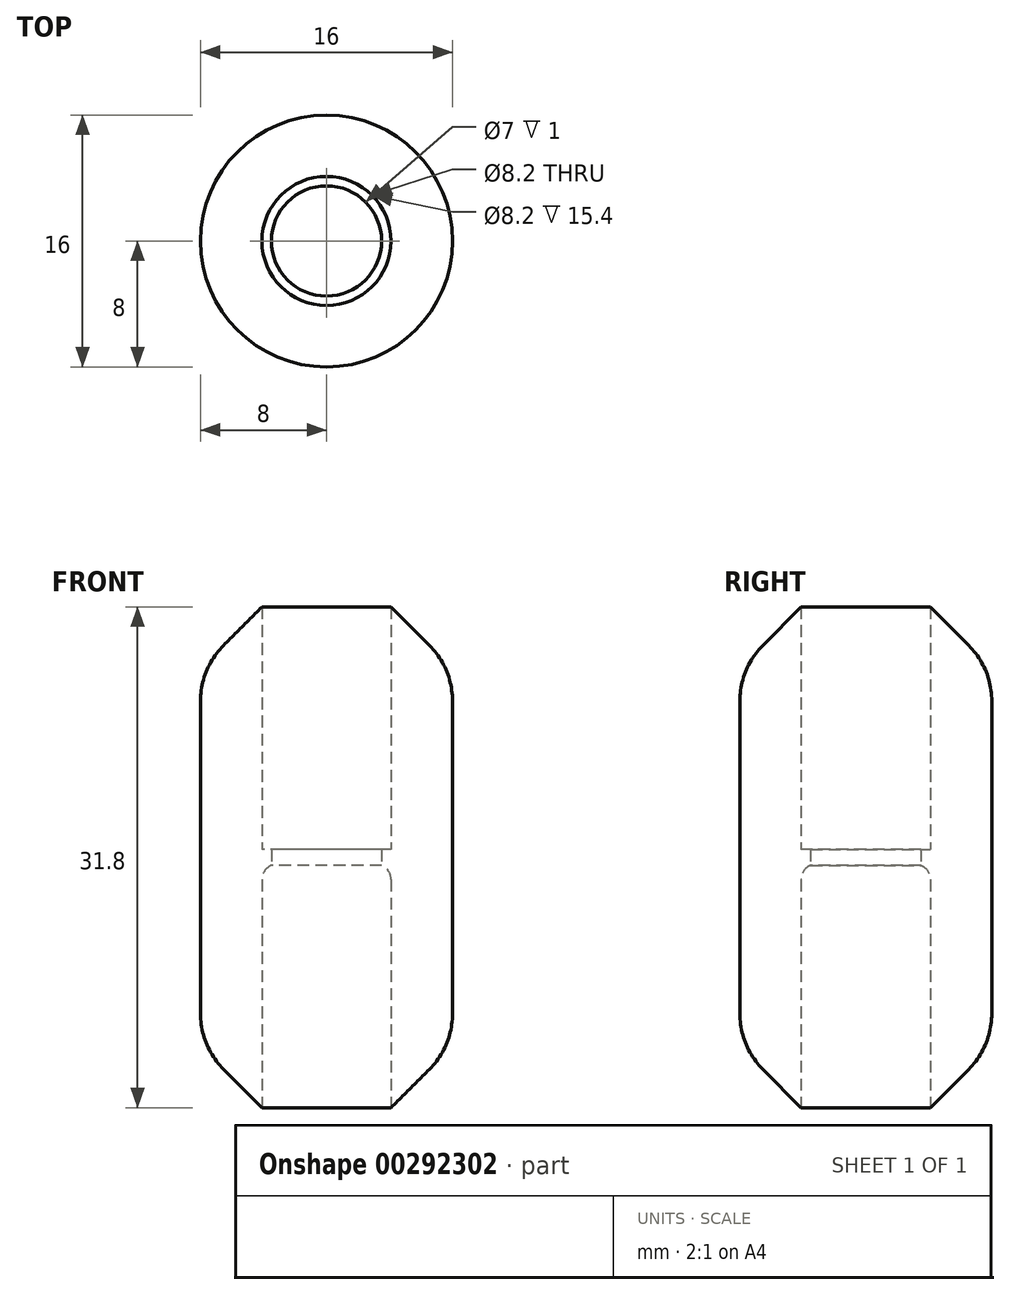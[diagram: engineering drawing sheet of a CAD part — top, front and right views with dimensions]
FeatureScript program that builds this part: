
annotation { "Feature Type Name" : "Feature", "Feature Type Description" : "" }
export const myFeature = defineFeature(function(context is Context, id is Id, definition is map)
    precondition{}
    {
        {
            var Q0;
            Q0=qCreatedBy(makeId("Top.planeOp"),FACE);
            var sketch = newSketch(context, id + "F0", { "sketchPlane" : qUnion([Q0])});
            skCircle(sketch, "E0", {"center": v(0, 0) * mm, "radius": 4.1 * mm});
            skCircle(sketch, "E1", {"center": v(0, 0) * mm, "radius": 8 * mm});
            skCircle(sketch, "E2", {"center": v(0, 0) * mm, "radius": 3.5 * mm});
            skSolve(sketch);
        }
        {
            var Q0;
            Q0=makeQuery(id+"F0.imprint","IMPRINT",FACE,{"disambiguationData":[TD([[makeQuery(id+"F0.imprint","IMPRINT",EDGE,{"derivedFrom":sQuery(id+"F0.wireOp",EDGE,"E0")}),1.0]])]});
            extrude(context, id + "F1", {"entities" : qUnion([Q0]), "endBound" : BoundingType.SYMMETRIC, "depth" : 1 * mm});
        }
        {
            var Q0;
            Q0=makeQuery(id+"F0.imprint","IMPRINT",FACE,{"disambiguationData":[TD([[makeQuery(id+"F0.imprint","IMPRINT",EDGE,{"derivedFrom":sQuery(id+"F0.wireOp",EDGE,"E0")}),-1.0]])]});
            extrude(context, id + "F2", {"entities" : qUnion([Q0]), "operationType" : NewBodyOperationType.ADD, "endBound" : BoundingType.SYMMETRIC, "depth" : 32 * mm});
        }
        {
            var Q0;
            Q0=makeQuery(id+"F1.opExtrude","CAP_EDGE",EDGE,{"disambiguationData":[OSD([sQuery(id+"F0.wireOp",EDGE,"E0")])],"isStart":false});
            var Q1;
            Q1=makeQuery(id+"F1.opExtrude","CAP_EDGE",EDGE,{"disambiguationData":[OSD([sQuery(id+"F0.wireOp",EDGE,"E0")])],"isStart":true});
            fillet(context, id + "F3", {"entities" : qUnion([Q0, Q1]), "radius" : 1 * mm, "tangentPropagation" : true, "allowEdgeOverflow" : false});
        }
        {
            var Q0;
            Q0=makeQuery(id+"F2.opExtrude","CAP_EDGE",EDGE,{"disambiguationData":[OSD([sQuery(id+"F0.wireOp",EDGE,"E1")])],"isStart":true});
            var Q1;
            Q1=makeQuery(id+"F2.opExtrude","CAP_EDGE",EDGE,{"disambiguationData":[OSD([sQuery(id+"F0.wireOp",EDGE,"E1")])],"isStart":false});
            chamfer(context, id + "F4", {"entities" : qUnion([Q0, Q1]), "width" : 4 * mm, "tangentPropagation" : true});
        }
        {
            var Q0;
            {var subQ0=sQuery(id+"F0.wireOp",EDGE,"E1");Q0=makeQuery(id+"F4.opChamfer","BLEND_EDGE",EDGE,{"blendedFrom":[makeQuery(id+"F2.opExtrude","CAP_EDGE",EDGE,{"disambiguationData":[OSD([subQ0])],"isStart":true}),makeQuery(id+"F2.opExtrude","SWEPT_FACE",FACE,{"disambiguationData":[OSD([subQ0])]})],"blendedInto":[makeQuery(id+"F2.opExtrude","SWEPT_FACE",FACE,{"disambiguationData":[OSD([subQ0])]})]});}
            var Q1;
            {var subQ0=sQuery(id+"F0.wireOp",EDGE,"E1");Q1=makeQuery(id+"F4.opChamfer","BLEND_EDGE",EDGE,{"blendedFrom":[makeQuery(id+"F2.opExtrude","CAP_EDGE",EDGE,{"disambiguationData":[OSD([subQ0])],"isStart":false}),makeQuery(id+"F2.opExtrude","SWEPT_FACE",FACE,{"disambiguationData":[OSD([subQ0])]})],"blendedInto":[makeQuery(id+"F2.opExtrude","SWEPT_FACE",FACE,{"disambiguationData":[OSD([subQ0])]})]});}
            fillet(context, id + "F5", {"entities" : qUnion([Q0, Q1]), "radius" : 5 * mm, "tangentPropagation" : true, "allowEdgeOverflow" : false});
        }
    });
